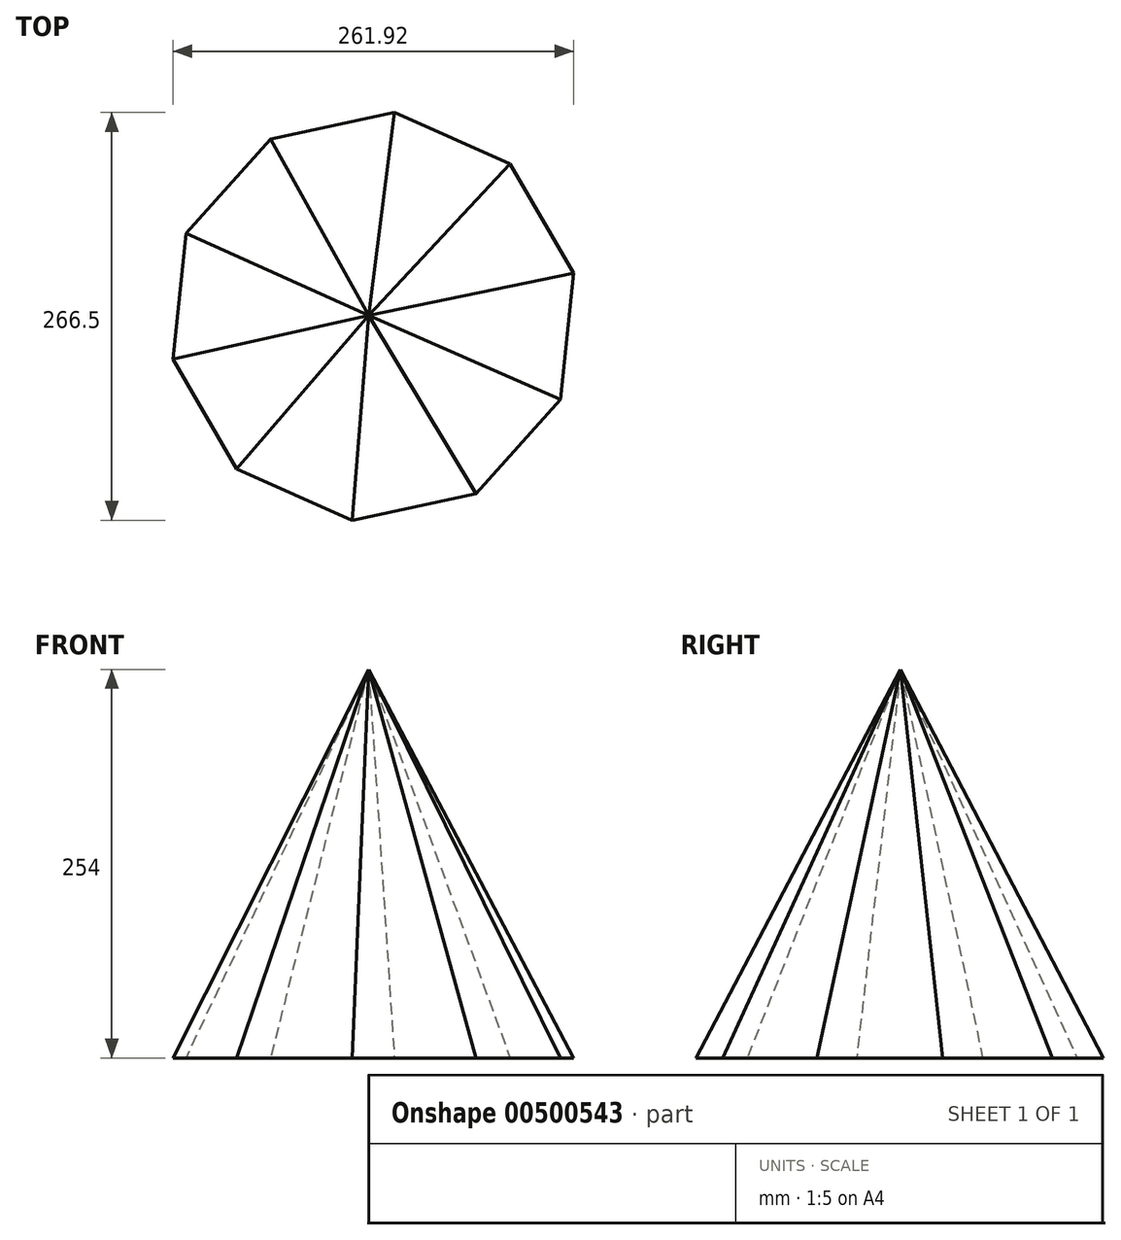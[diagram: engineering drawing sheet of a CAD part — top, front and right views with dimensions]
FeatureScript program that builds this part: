
annotation { "Feature Type Name" : "Feature", "Feature Type Description" : "" }
export const myFeature = defineFeature(function(context is Context, id is Id, definition is map)
    precondition{}
    {
        {
            var Q0;
            Q0=qCreatedBy(makeId("Top.planeOp"),FACE);
            var sketch = newSketch(context, id + "F0", { "sketchPlane" : qUnion([Q0])});
            skCircle(sketch, "E0.cCircle", {"center": v(0, 0) * mm, "radius": 133.95 * mm, "construction": true});
            skLineSegment(sketch, "E0.0", {"start": v(-67.24, 115.85) * mm, "end": v(13.7, 133.25) * mm});
            skLineSegment(sketch, "E0.1", {"start": v(13.7, 133.25) * mm, "end": v(89.4, 99.75) * mm});
            skLineSegment(sketch, "E0.2", {"start": v(89.4, 99.75) * mm, "end": v(130.96, 28.15) * mm});
            skLineSegment(sketch, "E0.3", {"start": v(130.96, 28.15) * mm, "end": v(122.5, -54.2) * mm});
            skLineSegment(sketch, "E0.4", {"start": v(122.5, -54.2) * mm, "end": v(67.24, -115.85) * mm});
            skLineSegment(sketch, "E0.5", {"start": v(67.24, -115.85) * mm, "end": v(-13.7, -133.25) * mm});
            skLineSegment(sketch, "E0.6", {"start": v(-13.7, -133.25) * mm, "end": v(-89.4, -99.75) * mm});
            skLineSegment(sketch, "E0.7", {"start": v(-89.4, -99.75) * mm, "end": v(-130.96, -28.15) * mm});
            skLineSegment(sketch, "E0.8", {"start": v(-130.96, -28.15) * mm, "end": v(-122.5, 54.2) * mm});
            skLineSegment(sketch, "E0.9", {"start": v(-122.5, 54.2) * mm, "end": v(-67.24, 115.85) * mm});
            skSolve(sketch);
        }
        {
            var Q0;
            Q0=qCreatedBy(makeId("Top.planeOp"),FACE);
            cPlane(context, id + "F1", {"entities" : qUnion([Q0]), "cplaneType" : CPlaneType.OFFSET, "offset" : 254 * mm, "width" : 152.4 * mm, "height" : 152.4 * mm});
        }
        {
            var Q0;
            Q0=qCreatedBy(id+"F1.planeOp",FACE);
            var sketch = newSketch(context, id + "F2", { "sketchPlane" : qUnion([Q0])});
            skPoint(sketch, "E1", {"position": v(-3, 0.5) * mm});
            skSolve(sketch);
        }
        {
            var Q0;
            Q0=sQuery(id+"F2.wireOp",VERTEX,"E1");
            var Q1;
            Q1=makeQuery(id+"F0.imprint","IMPRINT",FACE,{"disambiguationData":[TD([[makeQuery(id+"F0.imprint","IMPRINT",EDGE,{"derivedFrom":sQuery(id+"F0.wireOp",EDGE,"E0.0")}),-1.0]])]});
            loft(context, id + "F3", {"sheetProfilesArray" : [{ "sheetProfileEntities" : qUnion([Q0]) }, { "sheetProfileEntities" : qUnion([Q1]) }]});
        }
    });
